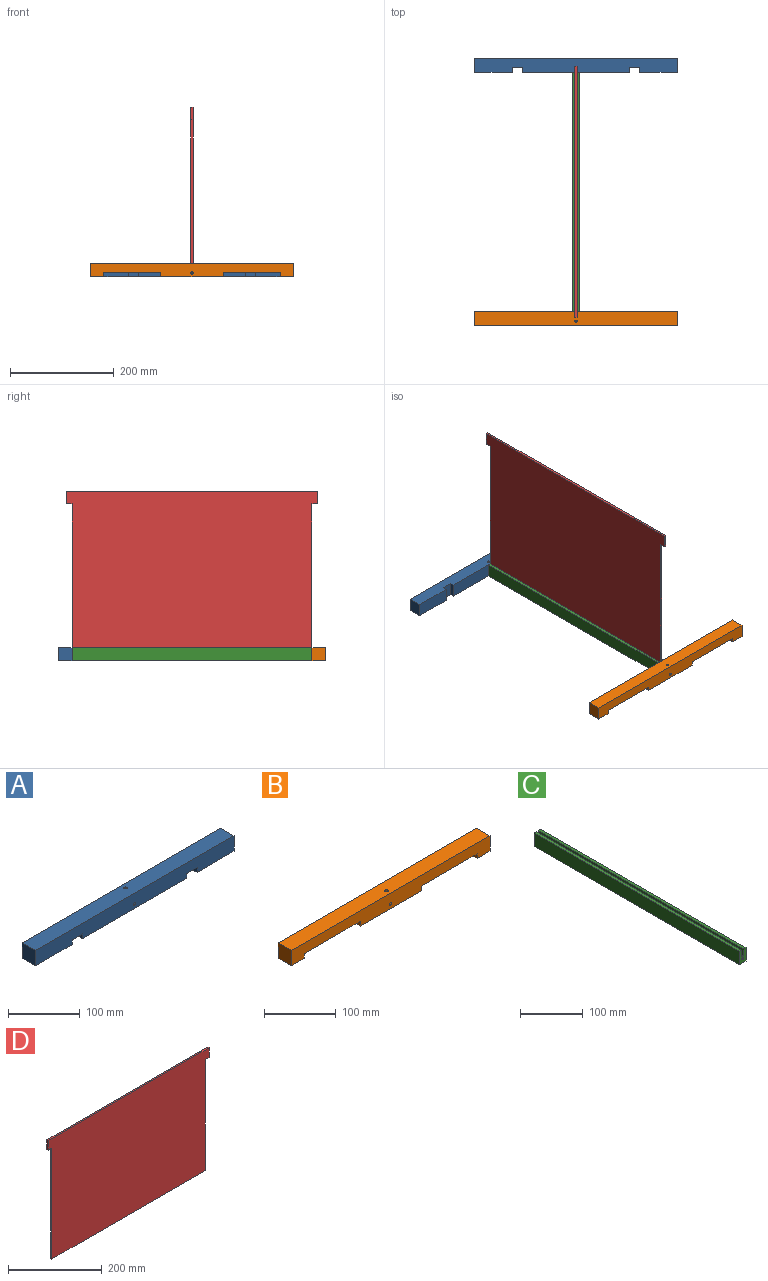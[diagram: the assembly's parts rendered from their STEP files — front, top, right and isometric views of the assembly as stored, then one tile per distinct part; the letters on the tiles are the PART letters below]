
ASSEMBLY  parts=4 mates=3
PART A: 18 faces, bbox 391x26x26 mm
  f0: plane 72.75x26mm, normal (0,0,-1), area 1891.5mm2, adj f1,f2,f8,f15
  f1: plane 391x26mm, normal (0,-1,0), area 9830.1mm2, adj f0,f3,f4,f6,f7,f8,f9,f12
  f2: plane 391x26mm, normal (0,1,0), area 9830.1mm2, adj f0,f3,f5,f6,f7,f8,f9,f12
  f3: plane 205.5x26mm, normal (0,0,-1), area 5327.1mm2, adj f1,f2,f10,f12,f17
  f4: cylinder r=2.25mm len=18mm, axis (0,-1,0), area 234.2mm2, adj f1,f10,f11
  f5: cylinder r=2.25mm len=8mm, axis (0,-1,0), area 92.8mm2, adj f2,f10,f11
  f6: plane 391x26mm, normal (0,0,1), area 10150.1mm2, adj f1,f2,f8,f9,f11
  f7: plane 72.75x26mm, normal (0,0,-1), area 1891.5mm2, adj f1,f2,f9,f14
  f8: plane 26x26mm, normal (1,0,0), area 676mm2, adj f0,f1,f2,f6
  f9: plane 26x26mm, normal (-1,0,0), area 676mm2, adj f1,f2,f6,f7
  f10: cylinder r=2.25mm len=8mm, axis (0,0,-1), area 92.8mm2, adj f3,f4,f5
  f11: cylinder r=2.25mm len=18mm, axis (0,0,-1), area 234.2mm2, adj f4,f5,f6
  f12: plane 26x8mm, normal (-1,0,0), area 208mm2, adj f1,f2,f3,f13
  f13: plane 26x20mm, normal (0,0,-1), area 520mm2, adj f1,f2,f12,f14
  f14: plane 26x8mm, normal (1,0,0), area 208mm2, adj f1,f2,f7,f13
  f15: plane 26x8mm, normal (-1,0,0), area 208mm2, adj f0,f1,f2,f16
  f16: plane 26x20mm, normal (0,0,-1), area 520mm2, adj f1,f2,f15,f17
  f17: plane 26x8mm, normal (1,0,0), area 208mm2, adj f1,f2,f3,f16
PART B: 18 faces, bbox 391x26x26 mm
  f0: cylinder r=2.25mm len=8mm, axis (0,-1,0), area 92.8mm2, adj f3,f16,f17
  f1: cylinder r=2.25mm len=18mm, axis (0,-1,0), area 234.2mm2, adj f4,f16,f17
  f2: plane 26x25.5mm, normal (0,0,-1), area 663mm2, adj f3,f4,f8,f14
  f3: plane 391x26mm, normal (0,-1,0), area 8390.1mm2, adj f0,f2,f5,f6,f7,f8,f9,f10
  f4: plane 391x26mm, normal (0,1,0), area 8390.1mm2, adj f1,f2,f5,f6,f7,f8,f9,f10
  f5: plane 120x26mm, normal (0,0,-1), area 3104.1mm2, adj f3,f4,f10,f13,f17
  f6: plane 391x26mm, normal (0,0,1), area 10150.1mm2, adj f3,f4,f8,f9,f16
  f7: plane 26x25.5mm, normal (0,0,-1), area 663mm2, adj f3,f4,f9,f12
  f8: plane 26x26mm, normal (1,0,0), area 676mm2, adj f2,f3,f4,f6
  f9: plane 26x26mm, normal (-1,0,0), area 676mm2, adj f3,f4,f6,f7
  f10: plane 26x8mm, normal (-1,0,0), area 208mm2, adj f3,f4,f5,f11
  f11: plane 110x26mm, normal (0,0,-1), area 2860mm2, adj f3,f4,f10,f12
  f12: plane 26x8mm, normal (1,0,0), area 208mm2, adj f3,f4,f7,f11
  f13: plane 26x8mm, normal (1,0,0), area 208mm2, adj f3,f4,f5,f15
  f14: plane 26x8mm, normal (-1,0,0), area 208mm2, adj f2,f3,f4,f15
  f15: plane 110x26mm, normal (0,0,-1), area 2860mm2, adj f3,f4,f13,f14
  f16: cylinder r=2.25mm len=18mm, axis (0,0,1), area 234.2mm2, adj f0,f1,f6
  f17: cylinder r=2.25mm len=8mm, axis (0,0,1), area 92.8mm2, adj f0,f1,f5
PART C: 14 faces, bbox 15x463x26 mm
  f0: plane 463x15mm, normal (0,0,-1), area 6945mm2, adj f1,f7,f8,f9
  f1: plane 463x26mm, normal (1,0,0), area 12038mm2, adj f0,f2,f8,f9
  f2: plane 463x5mm, normal (0,0,1), area 2315mm2, adj f1,f3,f8,f9
  f3: plane 463x13mm, normal (-1,0,0), area 6019mm2, adj f2,f4,f8,f9
  f4: plane 463x5mm, normal (0,0,1), area 2315mm2, adj f3,f5,f8,f9
  f5: plane 463x13mm, normal (1,0,0), area 6019mm2, adj f4,f6,f8,f9
  f6: plane 463x5mm, normal (0,0,1), area 2315mm2, adj f5,f7,f8,f9
  f7: plane 463x26mm, normal (-1,0,0), area 12038mm2, adj f0,f6,f8,f9
  f8: plane 26x15mm, normal (0,-1,0), area 312.4mm2, adj f0,f1,f2,f3,f4,f5,f6,f7
  f9: plane 26x15mm, normal (0,1,0), area 312.4mm2, adj f0,f1,f2,f3,f4,f5,f6,f7
  f10: cone r=0mm half-angle=59deg, axis (0,-1,0), area 14.7mm2, adj f11
  f11: cylinder r=2mm len=15mm, axis (0,-1,0), area 188.5mm2, adj f8,f10
  f12: cone r=0mm half-angle=59deg, axis (0,1,0), area 14.7mm2, adj f13
  f13: cylinder r=2mm len=15mm, axis (0,1,0), area 188.5mm2, adj f9,f12
PART D: 10 faces, bbox 485x4x315 mm
  f0: plane 25x4mm, normal (1,0,0), area 100mm2, adj f1,f7,f8,f9
  f1: plane 485x4mm, normal (0,0,1), area 1940mm2, adj f0,f2,f8,f9
  f2: plane 25x4mm, normal (-1,0,0), area 100mm2, adj f1,f3,f8,f9
  f3: plane 11x4mm, normal (0,0,-1), area 44mm2, adj f2,f4,f8,f9
  f4: plane 290x4mm, normal (-1,0,0), area 1160mm2, adj f3,f5,f8,f9
  f5: plane 463x4mm, normal (0,0,-1), area 1852mm2, adj f4,f6,f8,f9
  f6: plane 290x4mm, normal (1,0,0), area 1160mm2, adj f5,f7,f8,f9
  f7: plane 11x4mm, normal (0,0,-1), area 44mm2, adj f0,f6,f8,f9
  f8: plane 485x315mm, normal (0,-1,0), area 146395mm2, adj f0,f1,f2,f3,f4,f5,f6,f7
  f9: plane 485x315mm, normal (0,1,0), area 146395mm2, adj f0,f1,f2,f3,f4,f5,f6,f7
PLACE A rot(axis=(-1,0,0),90deg) t=(0,231.5,13)mm
PLACE B t=(0,-244.5,0)mm
PLACE C at identity
PLACE D rot(axis=(0,0,-1),90deg) t=(0,0,13)mm
MATE fastened A.f2 <-> C.f0  axis (0,0,-1) through (0,231.5,0)mm
MATE fastened D.f5 <-> C.f4  axis (0,0,-1) through (0,-231.5,13)mm
MATE fastened C.f0 <-> B.f5  axis (0,0,-1) through (0,-231.5,0)mm
